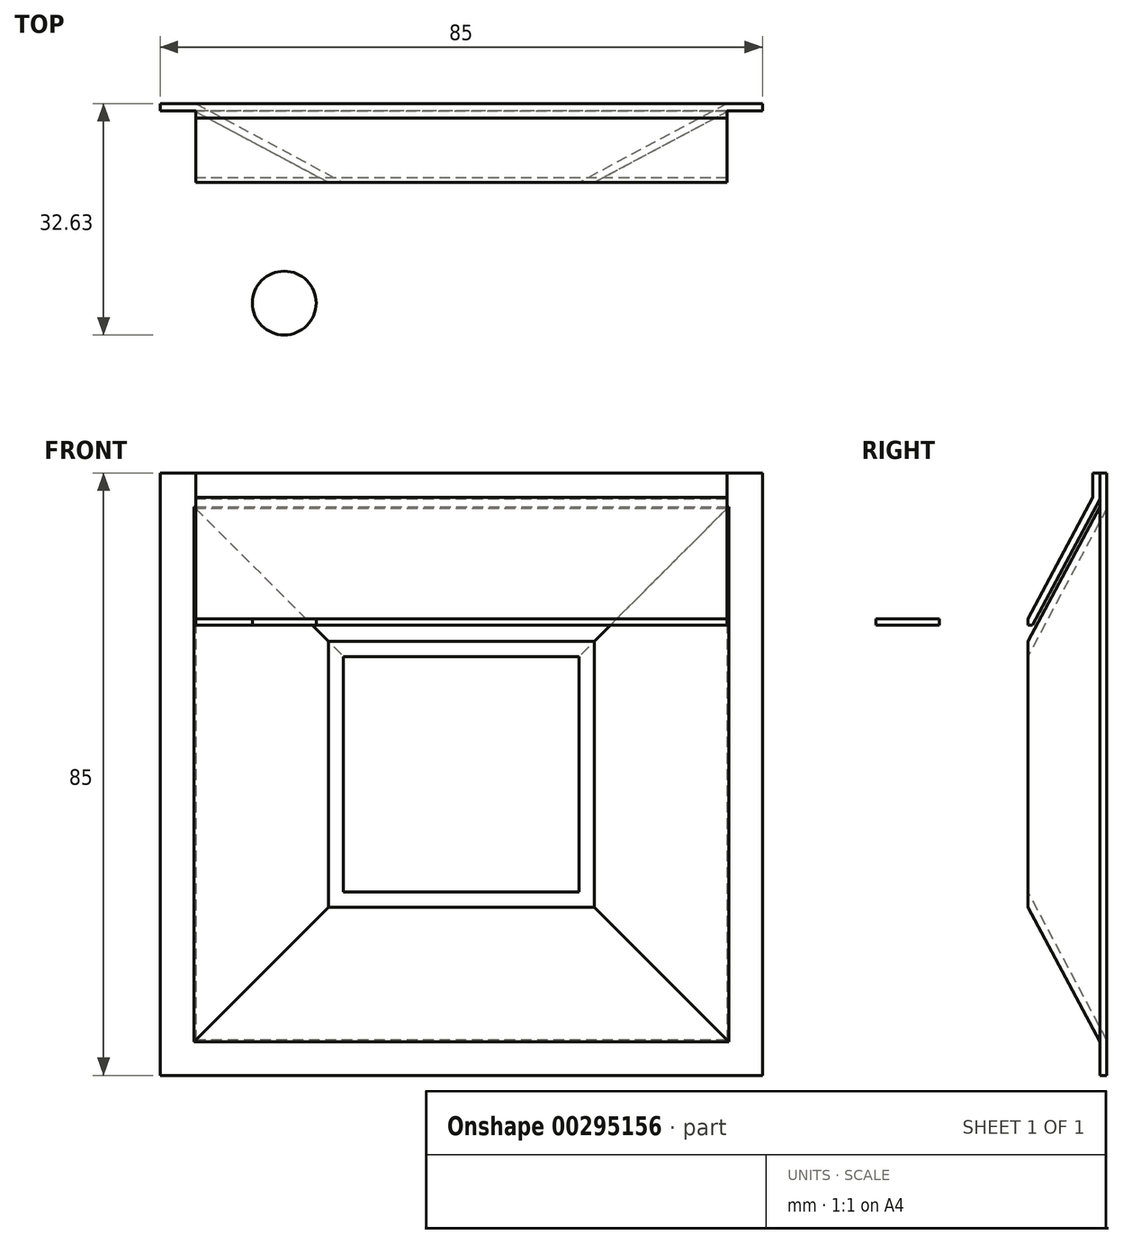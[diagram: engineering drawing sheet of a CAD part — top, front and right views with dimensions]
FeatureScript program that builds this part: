
annotation { "Feature Type Name" : "Feature", "Feature Type Description" : "" }
export const myFeature = defineFeature(function(context is Context, id is Id, definition is map)
    precondition{}
    {
        {
            var Q0;
            Q0=qCreatedBy(makeId("Front.planeOp"),FACE);
            var sketch = newSketch(context, id + "F0", { "sketchPlane" : qUnion([Q0])});
            skLineSegment(sketch, "E0.bottom", {"start": v(37.5, 37.5) * mm, "end": v(-37.5, 37.5) * mm});
            skLineSegment(sketch, "E0.top", {"start": v(37.5, -37.5) * mm, "end": v(-37.5, -37.5) * mm});
            skLineSegment(sketch, "E0.left", {"start": v(37.5, 37.5) * mm, "end": v(37.5, -37.5) * mm});
            skLineSegment(sketch, "E0.right", {"start": v(-37.5, 37.5) * mm, "end": v(-37.5, -37.5) * mm});
            skPoint(sketch, "E0.middle", {"position": v(0, 0) * mm});
            skLineSegment(sketch, "E1.0", {"start": v(42.5, 42.5) * mm, "end": v(-42.5, 42.5) * mm});
            skLineSegment(sketch, "E1.1", {"start": v(42.5, 42.5) * mm, "end": v(42.5, -42.5) * mm});
            skLineSegment(sketch, "E1.2", {"start": v(42.5, -42.5) * mm, "end": v(-42.5, -42.5) * mm});
            skLineSegment(sketch, "E1.3", {"start": v(-42.5, 42.5) * mm, "end": v(-42.5, -42.5) * mm});
            skSolve(sketch);
        }
        {
            var Q0;
            Q0=qCreatedBy(makeId("Front.planeOp"),FACE);
            cPlane(context, id + "F1", {"entities" : qUnion([Q0]), "cplaneType" : CPlaneType.OFFSET, "offset" : 20 * mm, "width" : 150 * mm, "height" : 150 * mm});
        }
        {
            var Q0;
            Q0=qCreatedBy(id+"F1.planeOp",FACE);
            var sketch = newSketch(context, id + "F2", { "sketchPlane" : qUnion([Q0])});
            skPoint(sketch, "E2", {"position": v(0, 0) * mm});
            skSolve(sketch);
        }
        {
            var Q0;
            Q0=makeQuery(id+"F0.imprint","IMPRINT",FACE,{"disambiguationData":[TD([[makeQuery(id+"F0.imprint","IMPRINT",EDGE,{"derivedFrom":sQuery(id+"F0.wireOp",EDGE,"E0.bottom")}),1.0]])]});
            var Q1;
            Q1=sQuery(id+"F2.wireOp",VERTEX,"E2");
            loft(context, id + "F3", {"sheetProfilesArray" : [{ "sheetProfileEntities" : qUnion([Q0]) }, { "sheetProfileEntities" : qUnion([Q1]) }]});
        }
        {
            var Q0;
            Q0=makeQuery(id+"F3.opLoft","CAP_FACE",FACE,{"disambiguationData":[OSD([makeQuery(id+"F0.imprint","IMPRINT",FACE,{"disambiguationData":[TD([[makeQuery(id+"F0.imprint","IMPRINT",EDGE,{"derivedFrom":sQuery(id+"F0.wireOp",EDGE,"E0.bottom")}),1.0]])]})])],"isStart":true});
            shell(context, id + "F4", {"entities" : qUnion([Q0]), "thickness" : 1 * mm, "oppositeDirection" : true});
        }
        {
            var Q0;
            Q0=makeQuery(id+"F0.imprint","IMPRINT",FACE,{"disambiguationData":[TD([[makeQuery(id+"F0.imprint","IMPRINT",EDGE,{"derivedFrom":sQuery(id+"F0.wireOp",EDGE,"E0.bottom")}),-1.0]])]});
            extrude(context, id + "F5", {"entities" : qUnion([Q0]), "operationType" : NewBodyOperationType.ADD, "depth" : 1 * mm});
        }
        {
            var Q0;
            Q0=qCreatedBy(makeId("Right.planeOp"),FACE);
            var sketch = newSketch(context, id + "F6", { "sketchPlane" : qUnion([Q0])});
            skLineSegment(sketch, "E3", {"start": v(-1, 37.75) * mm, "end": v(-21.13, 0) * mm});
            skLineSegment(sketch, "E4", {"start": v(-1, -37.75) * mm, "end": v(-1, -42.5) * mm});
            skLineSegment(sketch, "E5", {"start": v(-1, 42.5) * mm, "end": v(-1, 37.75) * mm});
            skLineSegment(sketch, "E6", {"start": v(-1, 42.5) * mm, "end": v(-2, 42.5) * mm});
            skLineSegment(sketch, "E7", {"start": v(-2, 42.5) * mm, "end": v(-2, 39.06) * mm});
            skLineSegment(sketch, "E8", {"start": v(-2, 39.06) * mm, "end": v(-11.13, 21.94) * mm});
            skLineSegment(sketch, "E9", {"start": v(-11.13, 21.94) * mm, "end": v(-36.13, 21.94) * mm});
            skLineSegment(sketch, "E10", {"start": v(-21.13, 0) * mm, "end": v(-21.13, 35.71) * mm, "construction": true});
            skLineSegment(sketch, "E11", {"start": v(-36.13, 21.94) * mm, "end": v(-36.13, 21.04) * mm});
            skLineSegment(sketch, "E12", {"start": v(-36.13, 21.04) * mm, "end": v(-10.48, 21.04) * mm});
            skLineSegment(sketch, "E13", {"start": v(-10.48, 21.04) * mm, "end": v(-1, 38.81) * mm});
            skLineSegment(sketch, "E14", {"start": v(-1, 38.81) * mm, "end": v(-1, 41.5) * mm});
            skLineSegment(sketch, "E15", {"start": v(-1, 41.5) * mm, "end": v(-1, 41.5) * mm});
            skSolve(sketch);
        }
        {
            var Q0;
            {var subQ0=sQuery(id+"F6.wireOp",EDGE,"E6");Q0=makeQuery(id+"F6.imprint","IMPRINT",FACE,{"disambiguationData":[TD([[makeQuery(id+"F6.imprint","IMPRINT",EDGE,{"derivedFrom":subQ0}),1.0]])]});}
            extrude(context, id + "F7", {"entities" : qUnion([Q0]), "operationType" : NewBodyOperationType.ADD, "endBound" : BoundingType.SYMMETRIC, "depth" : 75 * mm});
        }
        {
            var Q0;
            Q0=makeQuery(id+"F7.opExtrude","SWEPT_FACE",FACE,{"disambiguationData":[OSD([sQuery(id+"F6.wireOp",EDGE,"E9")])]});
            var sketch = newSketch(context, id + "F8", { "sketchPlane" : qUnion([Q0])});
            skCircle(sketch, "E16", {"center": v(25, -28.13) * mm, "radius": 4.5 * mm});
            skCircle(sketch, "E17.MirrorC", {"center": v(-25, -28.13) * mm, "radius": 4.5 * mm});
            skSolve(sketch);
        }
        {
            var Q0;
            Q0=makeQuery(id+"F8.imprint","IMPRINT",FACE,{"disambiguationData":[TD([[makeQuery(id+"F8.imprint","IMPRINT",EDGE,{"derivedFrom":sQuery(id+"F8.wireOp",EDGE,"E16")}),1.0]])]});
            var Q1;
            Q1=makeQuery(id+"F8.imprint","IMPRINT",FACE,{"disambiguationData":[TD([[makeQuery(id+"F8.imprint","IMPRINT",EDGE,{"derivedFrom":sQuery(id+"F8.wireOp",EDGE,"E17.MirrorC")}),-1.0]])]});
            extrude(context, id + "F9", {"entities" : qUnion([Q0, Q1]), "operationType" : NewBodyOperationType.REMOVE, "oppositeDirection" : true, "depth" : 51.8 * mm});
        }
    });
